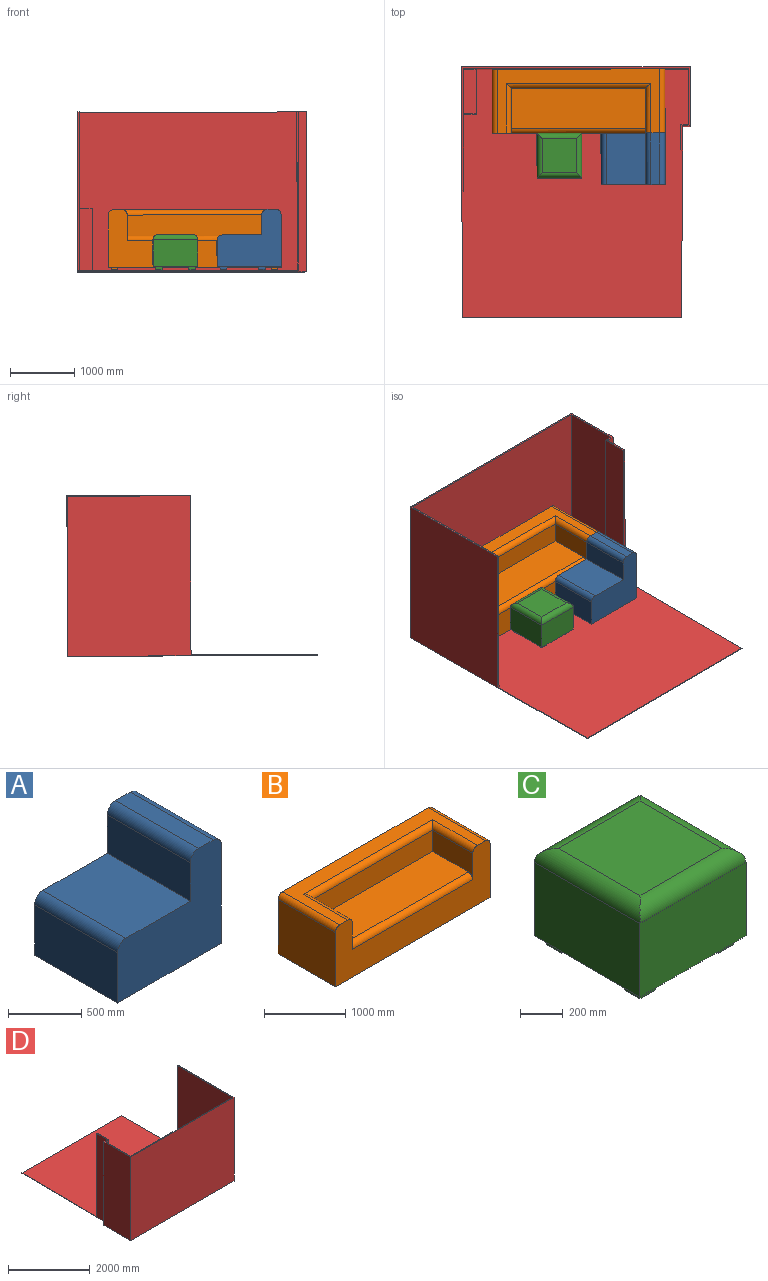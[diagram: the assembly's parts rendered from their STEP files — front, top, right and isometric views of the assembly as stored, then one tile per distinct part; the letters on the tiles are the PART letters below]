
ASSEMBLY  parts=4 mates=3
PART A: 31 faces, bbox 1000x800x940 mm
  f0: plane 1000x800mm, normal (0,0,-1), area 760000mm2, adj f1,f3,f4,f6,f11,f12,f13,f14
  f1: plane 1000x900mm, normal (0,1,0), area 615879.6mm2, adj f0,f2,f4,f5,f6,f7,f8,f9
  f2: plane 800x320mm, normal (-1,0,0), area 256000mm2, adj f1,f3,f7,f9
  f3: plane 1000x900mm, normal (0,-1,0), area 615879.6mm2, adj f0,f2,f4,f5,f6,f7,f8,f9
  f4: plane 820x800mm, normal (1,0,0), area 656000mm2, adj f0,f1,f3,f10
  f5: plane 800x140mm, normal (0,0,1), area 112000mm2, adj f1,f3,f9,f10
  f6: plane 800x420mm, normal (-1,0,0), area 336000mm2, adj f0,f1,f3,f8
  f7: plane 800x620mm, normal (0,0,1), area 496000mm2, adj f1,f2,f3,f8
  f8: cylinder r=80mm len=800mm, axis (0,1,0), area 100531mm2, adj f1,f3,f6,f7
  f9: cylinder r=80mm len=800mm, axis (0,1,0), area 100531mm2, adj f1,f2,f3,f5
  f10: cylinder r=80mm len=800mm, axis (0,-1,0), area 100531mm2, adj f1,f3,f4,f5
  f11: plane 100x40mm, normal (-1,0,0), area 4000mm2, adj f0,f12,f14,f15
  f12: plane 100x40mm, normal (0,-1,0), area 4000mm2, adj f0,f11,f13,f15
  f13: plane 100x40mm, normal (1,0,0), area 4000mm2, adj f0,f12,f14,f15
  f14: plane 100x40mm, normal (0,1,0), area 4000mm2, adj f0,f11,f13,f15
  f15: plane 100x100mm, normal (0,0,-1), area 10000mm2, adj f11,f12,f13,f14
  f16: plane 100x40mm, normal (0,1,0), area 4000mm2, adj f0,f17,f19,f20
  f17: plane 100x40mm, normal (-1,0,0), area 4000mm2, adj f0,f16,f18,f20
  f18: plane 100x40mm, normal (0,-1,0), area 4000mm2, adj f0,f17,f19,f20
  f19: plane 100x40mm, normal (1,0,0), area 4000mm2, adj f0,f16,f18,f20
  f20: plane 100x100mm, normal (0,0,-1), area 10000mm2, adj f16,f17,f18,f19
  f21: plane 100x40mm, normal (0,-1,0), area 4000mm2, adj f0,f22,f24,f25
  f22: plane 100x40mm, normal (1,0,0), area 4000mm2, adj f0,f21,f23,f25
  f23: plane 100x40mm, normal (0,1,0), area 4000mm2, adj f0,f22,f24,f25
  f24: plane 100x40mm, normal (-1,0,0), area 4000mm2, adj f0,f21,f23,f25
  f25: plane 100x100mm, normal (0,0,-1), area 10000mm2, adj f21,f22,f23,f24
  f26: plane 100x40mm, normal (1,0,0), area 4000mm2, adj f0,f27,f29,f30
  f27: plane 100x40mm, normal (0,1,0), area 4000mm2, adj f0,f26,f28,f30
  f28: plane 100x40mm, normal (-1,0,0), area 4000mm2, adj f0,f27,f29,f30
  f29: plane 100x40mm, normal (0,-1,0), area 4000mm2, adj f0,f26,f28,f30
  f30: plane 100x100mm, normal (0,0,-1), area 10000mm2, adj f26,f27,f28,f29
PART B: 36 faces, bbox 2700x1000x940 mm
  f0: plane 2700x1000mm, normal (0,0,-1), area 2660000mm2, adj f4,f5,f6,f7,f16,f17,f18,f19
  f1: plane 700x400mm, normal (1,0,0), area 225373.5mm2, adj f2,f4,f9,f10,f11
  f2: plane 2100x320mm, normal (0,-1,0), area 672000mm2, adj f1,f3,f9,f12
  f3: plane 700x400mm, normal (-1,0,0), area 225373.5mm2, adj f2,f4,f9,f10,f13
  f4: plane 2700x900mm, normal (0,-1,0), area 1416506.2mm2, adj f0,f1,f3,f5,f7,f8,f10,f11
  f5: plane 1000x820mm, normal (1,0,0), area 820000mm2, adj f0,f4,f6,f14
  f6: plane 2700x900mm, normal (0,1,0), area 2427253.1mm2, adj f0,f5,f7,f8,f14,f15
  f7: plane 1000x820mm, normal (-1,0,0), area 820000mm2, adj f0,f4,f6,f15
  f8: plane 2540x1000mm, normal (0,0,1), area 777200mm2, adj f4,f6,f11,f12,f13,f14,f15
  f9: plane 2100x620mm, normal (0,0,1), area 1302000mm2, adj f1,f2,f3,f10
  f10: cylinder r=80mm len=2100mm, axis (1,0,0), area 263893.8mm2, adj f1,f3,f4,f9
  f11: cylinder r=80mm len=780mm, axis (0,-1,0), area 91617.7mm2, adj f1,f4,f8,f12
  f12: cylinder r=80mm len=2260mm, axis (-1,0,0), area 271200mm2, adj f2,f8,f11,f13
  f13: cylinder r=80mm len=780mm, axis (0,1,0), area 91617.7mm2, adj f3,f4,f8,f12
  f14: cylinder r=80mm len=1000mm, axis (0,-1,0), area 125663.7mm2, adj f4,f5,f6,f8
  f15: cylinder r=80mm len=1000mm, axis (0,1,0), area 125663.7mm2, adj f4,f6,f7,f8
  f16: plane 100x40mm, normal (0,-1,0), area 4000mm2, adj f0,f17,f19,f20
  f17: plane 100x40mm, normal (1,0,0), area 4000mm2, adj f0,f16,f18,f20
  f18: plane 100x40mm, normal (0,1,0), area 4000mm2, adj f0,f17,f19,f20
  f19: plane 100x40mm, normal (-1,0,0), area 4000mm2, adj f0,f16,f18,f20
  f20: plane 100x100mm, normal (0,0,-1), area 10000mm2, adj f16,f17,f18,f19
  f21: plane 100x40mm, normal (0,1,0), area 4000mm2, adj f0,f22,f24,f25
  f22: plane 100x40mm, normal (-1,0,0), area 4000mm2, adj f0,f21,f23,f25
  f23: plane 100x40mm, normal (0,-1,0), area 4000mm2, adj f0,f22,f24,f25
  f24: plane 100x40mm, normal (1,0,0), area 4000mm2, adj f0,f21,f23,f25
  f25: plane 100x100mm, normal (0,0,-1), area 10000mm2, adj f21,f22,f23,f24
  f26: plane 100x40mm, normal (1,0,0), area 4000mm2, adj f0,f27,f29,f30
  f27: plane 100x40mm, normal (0,1,0), area 4000mm2, adj f0,f26,f28,f30
  f28: plane 100x40mm, normal (-1,0,0), area 4000mm2, adj f0,f27,f29,f30
  f29: plane 100x40mm, normal (0,-1,0), area 4000mm2, adj f0,f26,f28,f30
  f30: plane 100x100mm, normal (0,0,-1), area 10000mm2, adj f26,f27,f28,f29
  f31: plane 100x40mm, normal (-1,0,0), area 4000mm2, adj f0,f32,f34,f35
  f32: plane 100x40mm, normal (0,-1,0), area 4000mm2, adj f0,f31,f33,f35
  f33: plane 100x40mm, normal (1,0,0), area 4000mm2, adj f0,f32,f34,f35
  f34: plane 100x40mm, normal (0,1,0), area 4000mm2, adj f0,f31,f33,f35
  f35: plane 100x100mm, normal (0,0,-1), area 10000mm2, adj f31,f32,f33,f34
PART C: 30 faces, bbox 700x700x550 mm
  f0: plane 700x700mm, normal (0,0,-1), area 450000mm2, adj f1,f2,f3,f4,f10,f11,f12,f13
  f1: plane 700x420mm, normal (1,0,0), area 294000mm2, adj f0,f2,f4,f6
  f2: plane 700x420mm, normal (0,1,0), area 294000mm2, adj f0,f1,f3,f7
  f3: plane 700x420mm, normal (-1,0,0), area 294000mm2, adj f0,f2,f4,f9
  f4: plane 700x420mm, normal (0,-1,0), area 294000mm2, adj f0,f1,f3,f8
  f5: plane 540x540mm, normal (0,0,1), area 291600mm2, adj f6,f7,f8,f9
  f6: cylinder r=80mm len=700mm, axis (0,-1,0), area 80658.4mm2, adj f1,f5,f7,f8
  f7: cylinder r=80mm len=700mm, axis (1,0,0), area 80658.4mm2, adj f2,f5,f6,f9
  f8: cylinder r=80mm len=700mm, axis (-1,0,0), area 80658.4mm2, adj f4,f5,f6,f9
  f9: cylinder r=80mm len=700mm, axis (0,1,0), area 80658.4mm2, adj f3,f5,f7,f8
  f10: plane 100x50mm, normal (1,0,0), area 5000mm2, adj f0,f11,f13,f14
  f11: plane 100x50mm, normal (0,-1,0), area 5000mm2, adj f0,f10,f12,f14
  f12: plane 100x50mm, normal (-1,0,0), area 5000mm2, adj f0,f11,f13,f14
  f13: plane 100x50mm, normal (0,1,0), area 5000mm2, adj f0,f10,f12,f14
  f14: plane 100x100mm, normal (0,0,-1), area 10000mm2, adj f10,f11,f12,f13
  f15: plane 100x50mm, normal (0,-1,0), area 5000mm2, adj f0,f16,f18,f19
  f16: plane 100x50mm, normal (-1,0,0), area 5000mm2, adj f0,f15,f17,f19
  f17: plane 100x50mm, normal (0,1,0), area 5000mm2, adj f0,f16,f18,f19
  f18: plane 100x50mm, normal (1,0,0), area 5000mm2, adj f0,f15,f17,f19
  f19: plane 100x100mm, normal (0,0,-1), area 10000mm2, adj f15,f16,f17,f18
  f20: plane 100x50mm, normal (1,0,0), area 5000mm2, adj f0,f21,f23,f24
  f21: plane 100x50mm, normal (0,-1,0), area 5000mm2, adj f0,f20,f22,f24
  f22: plane 100x50mm, normal (-1,0,0), area 5000mm2, adj f0,f21,f23,f24
  f23: plane 100x50mm, normal (0,1,0), area 5000mm2, adj f0,f20,f22,f24
  f24: plane 100x100mm, normal (0,0,-1), area 10000mm2, adj f20,f21,f22,f23
  f25: plane 100x50mm, normal (-1,0,0), area 5000mm2, adj f0,f26,f28,f29
  f26: plane 100x50mm, normal (0,1,0), area 5000mm2, adj f0,f25,f27,f29
  f27: plane 100x50mm, normal (1,0,0), area 5000mm2, adj f0,f26,f28,f29
  f28: plane 100x50mm, normal (0,-1,0), area 5000mm2, adj f0,f25,f27,f29
  f29: plane 100x100mm, normal (0,0,-1), area 10000mm2, adj f25,f26,f27,f28
PART D: 30 faces, bbox 3570x3895x2501 mm
  f0: plane 3570x2500mm, normal (0,-1,0), area 8925000mm2, adj f1,f11,f12,f13
  f1: plane 3895x2501mm, normal (1,0,0), area 4834170mm2, adj f0,f2,f12,f13,f23,f24,f28,f29
  f2: plane 2490x25mm, normal (0,1,0), area 62250mm2, adj f1,f3,f12,f28
  f3: plane 2490x1900mm, normal (-1,0,0), area 4038000mm2, adj f2,f4,f12,f19,f20,f28
  f4: plane 3520x2490mm, normal (0,1,0), area 8566800mm2, adj f3,f5,f12,f18,f20,f28
  f5: plane 2490x870mm, normal (1,0,0), area 2166300mm2, adj f4,f6,f12,f28
  f6: plane 2490x120mm, normal (0,-1,0), area 298800mm2, adj f5,f7,f12,f28
  f7: plane 2490x400mm, normal (1,0,0), area 996000mm2, adj f6,f8,f12,f28
  f8: plane 2490x25mm, normal (0,1,0), area 62250mm2, adj f7,f9,f12,f28
  f9: plane 2500x375mm, normal (-1,0,0), area 937500mm2, adj f8,f10,f12,f13,f25
  f10: plane 2500x120mm, normal (0,1,0), area 300000mm2, adj f9,f11,f12,f13
  f11: plane 2500x920mm, normal (-1,0,0), area 2300000mm2, adj f0,f10,f12,f13
  f12: plane 3570x1925mm, normal (0,0,1), area 171500mm2, adj f0,f1,f2,f3,f4,f5,f6,f7
  f13: plane 3570x1925mm, normal (0,0,-1), area 311500mm2, adj f0,f1,f9,f10,f11,f14,f15,f16
  f14: plane 3320x1mm, normal (0,-1,0), area 3320mm2, adj f13,f17,f21,f29
  f15: plane 1200x1mm, normal (1,0,0), area 1200mm2, adj f13,f22,f23,f29
  f16: plane 120x1mm, normal (0,1,0), area 120mm2, adj f13,f17,f27,f29
  f17: plane 870x1mm, normal (-1,0,0), area 870mm2, adj f13,f14,f16,f29
  f18: plane 990x700mm, normal (-1,0,0), area 693000mm2, adj f4,f19,f20,f28
  f19: plane 990x200mm, normal (0,1,0), area 198000mm2, adj f3,f18,f20,f28
  f20: plane 700x200mm, normal (0,0,1), area 140000mm2, adj f3,f4,f18,f19
  f21: plane 700x1mm, normal (1,0,0), area 700mm2, adj f13,f14,f22,f29
  f22: plane 200x1mm, normal (0,-1,0), area 200mm2, adj f13,f15,f21,f29
  f23: plane 25x1mm, normal (0,-1,0), area 25mm2, adj f1,f13,f15,f29
  f24: plane 3425x11mm, normal (0,1,0), area 37675mm2, adj f1,f25,f28,f29
  f25: plane 2600x25mm, normal (-1,0.01,0), area 28601.3mm2, adj f9,f24,f26,f28,f29
  f26: plane 25x1mm, normal (0,-1,0), area 25mm2, adj f13,f25,f27,f29
  f27: plane 400x1mm, normal (-1,0,0), area 400mm2, adj f13,f16,f26,f29
  f28: plane 3870x3545mm, normal (0,0,1), area 13204150mm2, adj f1,f2,f3,f4,f5,f6,f7,f8
  f29: plane 3870x3545mm, normal (0,0,-1), area 13204150mm2, adj f1,f14,f15,f16,f17,f21,f22,f23
PLACE A rot(axis=(-0.91,-0.33,0.25),0.3deg) t=(9406.04,2761.36,-4243.42)mm
PLACE B rot(axis=(-0.91,-0.33,0.25),0.3deg) t=(8354.41,4160.12,-4250.84)mm
PLACE C rot(axis=(0,0,-1),179.9deg) t=(8055.97,2809.82,-4236.76)mm
PLACE D rot(axis=(0,0,-1),179.9deg) t=(10076.15,4161.83,-4321.09)mm
MATE fastened C.f4 <-> B.f4  axis (0,1,0) through (8055.24,3160.7,-4028.23)mm
MATE fastened B.f6 <-> D.f4  axis (0,1,0) through (8353.73,4162,-3801.33)mm
MATE fastened A.f1 <-> B.f4  axis (0,1,0) through (9704.95,3163.42,-3834.64)mm
